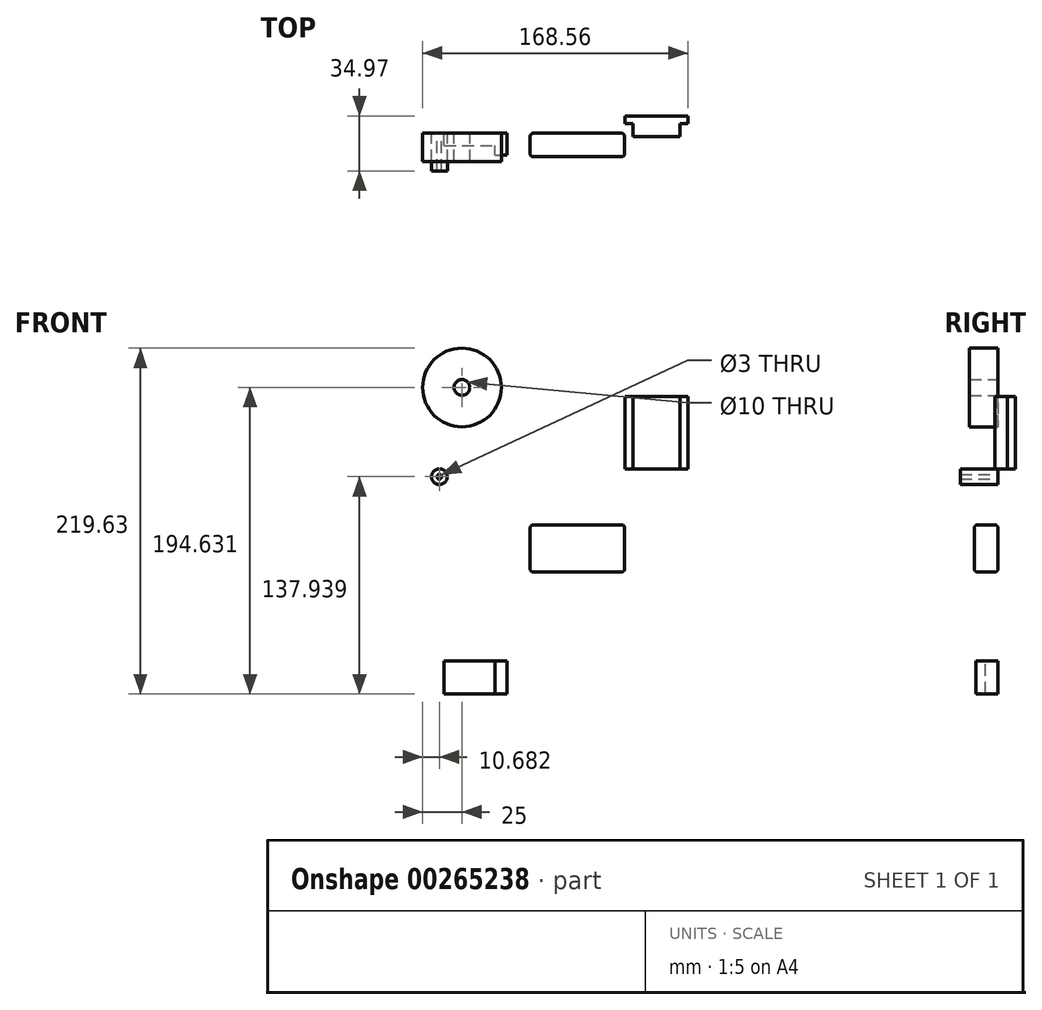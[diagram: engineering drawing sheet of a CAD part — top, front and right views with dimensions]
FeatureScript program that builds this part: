
annotation { "Feature Type Name" : "Feature", "Feature Type Description" : "" }
export const myFeature = defineFeature(function(context is Context, id is Id, definition is map)
    precondition{}
    {
        {
            var Q0;
            Q0=qCreatedBy(makeId("Front.planeOp"),FACE);
            var sketch = newSketch(context, id + "F0", { "sketchPlane" : qUnion([Q0])});
            skCircle(sketch, "E0", {"center": v(-49.92, 51.66) * mm, "radius": 25 * mm});
            skCircle(sketch, "E1", {"center": v(-49.92, 51.66) * mm, "radius": 5 * mm});
            skSolve(sketch);
        }
        {
            var Q0;
            Q0=makeQuery(id+"F0.imprint","IMPRINT",FACE,{"disambiguationData":[TD([[makeQuery(id+"F0.imprint","IMPRINT",EDGE,{"derivedFrom":sQuery(id+"F0.wireOp",EDGE,"E0")}),1.0]])]});
            extrude(context, id + "F1", {"entities" : qUnion([Q0]), "depth" : 18 * mm});
        }
        {
            var Q0;
            Q0=qCreatedBy(makeId("Front.planeOp"),FACE);
            var sketch = newSketch(context, id + "F2", { "sketchPlane" : qUnion([Q0])});
            skCircle(sketch, "E2", {"center": v(-64.24, -5.03) * mm, "radius": 5 * mm});
            skCircle(sketch, "E3", {"center": v(-64.24, -5.03) * mm, "radius": 1.5 * mm});
            skSolve(sketch);
        }
        {
            var Q0;
            Q0 = qSketchRegion(id + "F2", true);
            extrude(context, id + "F3", {"entities" : qUnion([Q0]), "depth" : 24 * mm});
        }
        {
            var Q0;
            Q0=qCreatedBy(makeId("Front.planeOp"),FACE);
            var sketch = newSketch(context, id + "F4", { "sketchPlane" : qUnion([Q0])});
            skLineSegment(sketch, "E4.bottom", {"start": v(53.43, -35.58) * mm, "end": v(-6.57, -35.58) * mm});
            skLineSegment(sketch, "E4.top", {"start": v(53.43, -65.58) * mm, "end": v(-6.57, -65.58) * mm});
            skLineSegment(sketch, "E4.left", {"start": v(53.43, -35.58) * mm, "end": v(53.43, -65.58) * mm});
            skLineSegment(sketch, "E4.right", {"start": v(-6.57, -35.58) * mm, "end": v(-6.57, -65.58) * mm});
            skSolve(sketch);
        }
        {
            var Q0;
            Q0 = qSketchRegion(id + "F4", true);
            extrude(context, id + "F5", {"entities" : qUnion([Q0]), "depth" : 15 * mm});
        }
        {
            var Q0;
            Q0=makeQuery(id+"F5.opExtrude","CAP_FACE",FACE,{"disambiguationData":[OSD([sQuery(id+"F4.wireOp",EDGE,"E4.bottom"),sQuery(id+"F4.wireOp",EDGE,"E4.top"),sQuery(id+"F4.wireOp",EDGE,"E4.left"),sQuery(id+"F4.wireOp",EDGE,"E4.right")])],"isStart":false});
            var Q1;
            Q1=makeQuery(id+"F5.opExtrude","CAP_FACE",FACE,{"disambiguationData":[OSD([sQuery(id+"F4.wireOp",EDGE,"E4.bottom"),sQuery(id+"F4.wireOp",EDGE,"E4.top"),sQuery(id+"F4.wireOp",EDGE,"E4.left"),sQuery(id+"F4.wireOp",EDGE,"E4.right")])],"isStart":true});
            var Q2;
            Q2=makeQuery(id+"F5.opExtrude","SWEPT_FACE",FACE,{"disambiguationData":[OSD([sQuery(id+"F4.wireOp",EDGE,"E4.top")])]});
            var Q3;
            Q3=makeQuery(id+"F5.opExtrude","SWEPT_FACE",FACE,{"disambiguationData":[OSD([sQuery(id+"F4.wireOp",EDGE,"E4.bottom")])]});
            fillet(context, id + "F6", {"entities" : qUnion([Q0, Q1, Q2, Q3]), "radius" : 2 * mm, "tangentPropagation" : true, "allowEdgeOverflow" : false});
        }
        {
            var Q0;
            Q0=qCreatedBy(makeId("Front.planeOp"),FACE);
            var sketch = newSketch(context, id + "F7", { "sketchPlane" : qUnion([Q0])});
            skLineSegment(sketch, "E5.bottom", {"start": v(-61.23, -121.97) * mm, "end": v(-21.23, -121.97) * mm});
            skLineSegment(sketch, "E5.top", {"start": v(-61.23, -142.97) * mm, "end": v(-21.23, -142.97) * mm});
            skLineSegment(sketch, "E5.left", {"start": v(-61.23, -121.97) * mm, "end": v(-61.23, -142.97) * mm});
            skLineSegment(sketch, "E5.right", {"start": v(-21.23, -121.97) * mm, "end": v(-21.23, -142.97) * mm});
            skSolve(sketch);
        }
        {
            var Q0;
            Q0 = qSketchRegion(id + "F7", true);
            extrude(context, id + "F8", {"entities" : qUnion([Q0]), "depth" : 8 * mm});
        }
        {
            var Q0;
            Q0=makeQuery(id+"F8.opExtrude","CAP_FACE",FACE,{"disambiguationData":[OSD([sQuery(id+"F7.wireOp",EDGE,"E5.bottom"),sQuery(id+"F7.wireOp",EDGE,"E5.top"),sQuery(id+"F7.wireOp",EDGE,"E5.left"),sQuery(id+"F7.wireOp",EDGE,"E5.right")])],"isStart":false});
            var sketch = newSketch(context, id + "F9", { "sketchPlane" : qUnion([Q0])});
            skLineSegment(sketch, "E6.bottom", {"start": v(-21.23, -142.97) * mm, "end": v(-28.77, -142.97) * mm});
            skLineSegment(sketch, "E6.top", {"start": v(-21.23, -121.97) * mm, "end": v(-28.77, -121.97) * mm});
            skLineSegment(sketch, "E6.left", {"start": v(-21.23, -142.97) * mm, "end": v(-21.23, -121.97) * mm});
            skLineSegment(sketch, "E6.right", {"start": v(-28.77, -142.97) * mm, "end": v(-28.77, -121.97) * mm});
            skSolve(sketch);
        }
        {
            var Q0;
            Q0 = qSketchRegion(id + "F9", true);
            extrude(context, id + "F10", {"entities" : qUnion([Q0]), "operationType" : NewBodyOperationType.ADD, "depth" : 6 * mm});
        }
        {
            var Q0;
            Q0=qCreatedBy(makeId("Top.planeOp"),FACE);
            var sketch = newSketch(context, id + "F11", { "sketchPlane" : qUnion([Q0])});
            skLineSegment(sketch, "E7", {"start": v(53.64, 10.97) * mm, "end": v(93.64, 10.97) * mm});
            skLineSegment(sketch, "E8", {"start": v(93.64, 10.97) * mm, "end": v(93.64, 5.97) * mm});
            skLineSegment(sketch, "E9", {"start": v(93.64, 5.97) * mm, "end": v(88.64, 5.97) * mm});
            skLineSegment(sketch, "E10", {"start": v(88.64, 5.97) * mm, "end": v(88.64, -2.03) * mm});
            skLineSegment(sketch, "E11", {"start": v(88.64, -2.03) * mm, "end": v(58.64, -2.03) * mm});
            skLineSegment(sketch, "E12", {"start": v(58.64, -2.03) * mm, "end": v(58.64, 5.97) * mm});
            skLineSegment(sketch, "E13", {"start": v(58.64, 5.97) * mm, "end": v(53.64, 5.97) * mm});
            skLineSegment(sketch, "E14", {"start": v(53.64, 5.97) * mm, "end": v(53.64, 10.97) * mm});
            skSolve(sketch);
        }
        {
            var Q0;
            Q0 = qSketchRegion(id + "F11", true);
            extrude(context, id + "F12", {"entities" : qUnion([Q0]), "depth" : 46 * mm});
        }
    });
